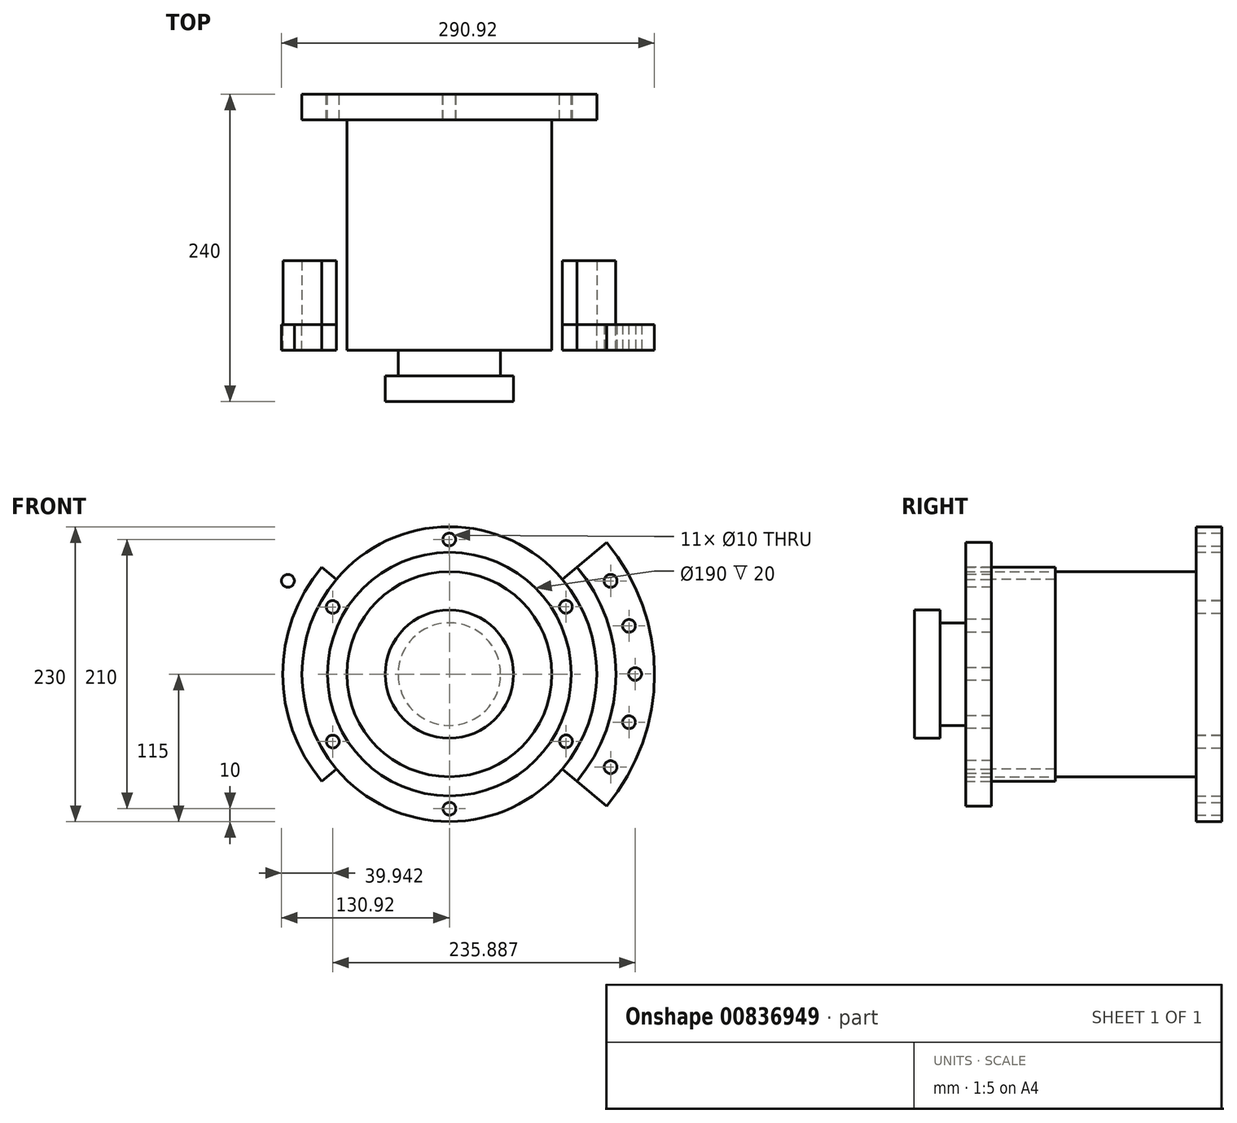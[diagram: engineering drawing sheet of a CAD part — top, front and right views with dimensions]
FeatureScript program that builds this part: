
annotation { "Feature Type Name" : "Feature", "Feature Type Description" : "" }
export const myFeature = defineFeature(function(context is Context, id is Id, definition is map)
    precondition{}
    {
        {
            var Q0;
            Q0=qCreatedBy(makeId("Front.planeOp"),FACE);
            var sketch = newSketch(context, id + "F0", { "sketchPlane" : qUnion([Q0])});
            skLineSegment(sketch, "E0", {"start": v(0, 0) * mm, "end": v(205.98, 0) * mm, "construction": true});
            skLineSegment(sketch, "E1", {"start": v(0, 0) * mm, "end": v(-190.1, -114.67) * mm, "construction": true});
            skLineSegment(sketch, "E2", {"start": v(189.9, 0.1) * mm, "end": v(-190.1, 0.1) * mm, "construction": true});
            skLineSegment(sketch, "E3", {"start": v(-0.1, 0.1) * mm, "end": v(-0.1, 105) * mm, "construction": true});
            skLineSegment(sketch, "E4.MirrorCS", {"start": v(189.9, 179.16) * mm, "end": v(189.9, -114.67) * mm, "construction": true});
            skCircle(sketch, "E5", {"center": v(144.9, 0.1) * mm, "radius": 5 * mm});
            skCircle(sketch, "E6", {"center": v(140.11, 37.67) * mm, "radius": 5 * mm});
            skCircle(sketch, "E7", {"center": v(125.73, 72.75) * mm, "radius": 5 * mm});
            skCircle(sketch, "E8.MirrorC", {"center": v(140.11, -37.46) * mm, "radius": 5 * mm});
            skCircle(sketch, "E9.MirrorC", {"center": v(125.73, -72.54) * mm, "radius": 5 * mm});
            skCircle(sketch, "E10.MirrorC", {"center": v(-125.92, 72.75) * mm, "radius": 5 * mm});
            skCircle(sketch, "E11.MirrorC", {"center": v(-140.3, 37.67) * mm, "radius": 5 * mm});
            skCircle(sketch, "E12.MirrorC", {"center": v(-145.1, 0.1) * mm, "radius": 5 * mm});
            skCircle(sketch, "E13.MirrorC", {"center": v(-140.3, -37.46) * mm, "radius": 5 * mm});
            skCircle(sketch, "E14.MirrorC", {"center": v(-125.92, -72.54) * mm, "radius": 5 * mm});
            skCircle(sketch, "E15", {"center": v(-0.1, 0.1) * mm, "radius": 145 * mm, "construction": true});
            skArc(sketch, "E16", {"start": v(-99.77, 83.56) * mm, "mid": v(-130.1, 0.02) * mm, "end": v(-99.66, -83.47) * mm});
            skLineSegment(sketch, "E17", {"start": v(79.9, 102.57) * mm, "end": v(79.9, 160.1) * mm, "construction": true});
            skLineSegment(sketch, "E18", {"start": v(79.9, 160.1) * mm, "end": v(-0.1, 160.1) * mm, "construction": true});
            skLineSegment(sketch, "E19.MirrorCS", {"start": v(-80.1, 160.1) * mm, "end": v(-0.1, 160.1) * mm, "construction": true});
            skLineSegment(sketch, "E20.MirrorCS", {"start": v(-80.1, 102.57) * mm, "end": v(-80.1, 160.1) * mm, "construction": true});
            skPoint(sketch, "E21.orphan", {"position": v(-80.1, 94.53) * mm});
            skPoint(sketch, "E22.orphan", {"position": v(79.9, 94.53) * mm});
            skLineSegment(sketch, "E23", {"start": v(-0.1, 0.1) * mm, "end": v(140.11, 37.67) * mm, "construction": true});
            skLineSegment(sketch, "E24", {"start": v(-0.1, 0.1) * mm, "end": v(125.73, 72.75) * mm, "construction": true});
            skCircle(sketch, "E25", {"center": v(0, 0) * mm, "radius": 65 * mm, "construction": true});
            skCircle(sketch, "E26", {"center": v(0, 0) * mm, "radius": 105 * mm, "construction": true});
            skCircle(sketch, "E27", {"center": v(-0.1, 105) * mm, "radius": 5 * mm});
            skCircle(sketch, "E28.1.0", {"center": v(-90.98, 52.42) * mm, "radius": 5 * mm});
            skCircle(sketch, "E28.2.0", {"center": v(-90.89, -52.58) * mm, "radius": 5 * mm});
            skCircle(sketch, "E28.3.0", {"center": v(0.1, -105) * mm, "radius": 5 * mm});
            skCircle(sketch, "E28.4.0", {"center": v(90.98, -52.42) * mm, "radius": 5 * mm});
            skCircle(sketch, "E28.5.0", {"center": v(90.89, 52.58) * mm, "radius": 5 * mm});
            skCircle(sketch, "E29", {"center": v(0, 0) * mm, "radius": 50 * mm});
            skLineSegment(sketch, "E30.trimOffspring", {"start": v(99.58, 83.56) * mm, "end": v(122.57, 102.85) * mm});
            skLineSegment(sketch, "E31.MirrorCS", {"start": v(99.48, -83.47) * mm, "end": v(122.57, -102.85) * mm});
            skArc(sketch, "E32.trimOffspring", {"start": v(122.57, -102.85) * mm, "mid": v(160, 0) * mm, "end": v(122.57, 102.85) * mm});
            skPoint(sketch, "E33.orphan", {"position": v(80.43, 67.5) * mm});
            skPoint(sketch, "E34.orphan", {"position": v(80.43, -67.5) * mm});
            skArc(sketch, "E35.MirrorCS", {"start": v(-122.75, -102.85) * mm, "mid": v(-160.18, 0) * mm, "end": v(-122.75, 102.85) * mm});
            skLineSegment(sketch, "E36.MirrorCS", {"start": v(-99.77, 83.56) * mm, "end": v(-122.75, 102.85) * mm});
            skLineSegment(sketch, "E37.MirrorCS", {"start": v(-99.66, -83.47) * mm, "end": v(-122.75, -102.85) * mm});
            skPoint(sketch, "E38.orphan", {"position": v(79.9, 102.57) * mm});
            skArc(sketch, "E39.trimOffspring", {"start": v(-99.66, -83.47) * mm, "mid": v(-129.38, 13.7) * mm, "end": v(-80.1, 102.57) * mm, "construction": true});
            skArc(sketch, "E40.MirrorCS", {"start": v(99.48, -83.47) * mm, "mid": v(129.9, 0.02) * mm, "end": v(99.58, 83.56) * mm});
            skCircle(sketch, "E41", {"center": v(0, 0) * mm, "radius": 115 * mm});
            skCircle(sketch, "E42", {"center": v(0, 0) * mm, "radius": 95 * mm});
            skSolve(sketch);
        }
        {
            var Q0;
            Q0=makeQuery(id+"F0.imprint","IMPRINT",FACE,{"disambiguationData":[TD([[makeQuery(id+"F0.imprint","IMPRINT",EDGE,{"derivedFrom":sQuery(id+"F0.wireOp",EDGE,"E5")}),-1.0]])]});
            var Q1;
            Q1=makeQuery(id+"F0.imprint","IMPRINT",FACE,{"disambiguationData":[TD([[makeQuery(id+"F0.imprint","IMPRINT",EDGE,{"derivedFrom":sQuery(id+"F0.wireOp",EDGE,"E10.MirrorC")}),1.0]])]});
            extrude(context, id + "F1", {"entities" : qUnion([Q0, Q1]), "oppositeDirection" : true, "depth" : 20 * mm, "offsetDistance" : 25 * mm});
        }
        {
            var Q0;
            Q0=makeQuery(id+"F1.opExtrude","CAP_FACE",FACE,{"disambiguationData":[OSD([sQuery(id+"F0.wireOp",EDGE,"E5"),sQuery(id+"F0.wireOp",EDGE,"E6"),sQuery(id+"F0.wireOp",EDGE,"E7"),sQuery(id+"F0.wireOp",EDGE,"E8.MirrorC"),sQuery(id+"F0.wireOp",EDGE,"E9.MirrorC"),sQuery(id+"F0.wireOp",EDGE,"E30.trimOffspring"),sQuery(id+"F0.wireOp",EDGE,"E31.MirrorCS"),sQuery(id+"F0.wireOp",EDGE,"E32.trimOffspring"),sQuery(id+"F0.wireOp",EDGE,"E40.MirrorCS")])],"isStart":false});
            cPlane(context, id + "F2", {"entities" : qUnion([Q0]), "cplaneType" : CPlaneType.OFFSET, "offset" : 180 * mm, "width" : 150 * mm, "height" : 150 * mm});
        }
        {
            var Q0;
            Q0=qCreatedBy(id+"F2.planeOp",FACE);
            var sketch = newSketch(context, id + "F3", { "sketchPlane" : qUnion([Q0])});
            skCircle(sketch, "E43.0", {"center": v(0, 0) * mm, "radius": 115 * mm});
            skCircle(sketch, "E44.0", {"center": v(0, 0) * mm, "radius": 95 * mm});
            skCircle(sketch, "E45.0", {"center": v(0, 0) * mm, "radius": 105 * mm, "construction": true});
            skCircle(sketch, "E46.0", {"center": v(0.1, 105) * mm, "radius": 5 * mm});
            skCircle(sketch, "E47.0", {"center": v(90.98, 52.42) * mm, "radius": 5 * mm});
            skCircle(sketch, "E48.0", {"center": v(90.89, -52.58) * mm, "radius": 5 * mm});
            skCircle(sketch, "E49.0", {"center": v(-90.89, 52.58) * mm, "radius": 5 * mm});
            skCircle(sketch, "E50.0", {"center": v(-90.98, -52.42) * mm, "radius": 5 * mm});
            skCircle(sketch, "E51.0", {"center": v(-0.1, -105) * mm, "radius": 5 * mm});
            skSolve(sketch);
        }
        {
            var Q0;
            Q0=makeQuery(id+"F3.imprint","IMPRINT",FACE,{"disambiguationData":[TD([[makeQuery(id+"F3.imprint","IMPRINT",EDGE,{"derivedFrom":sQuery(id+"F3.wireOp",EDGE,"E43.0")}),-1.0]])]});
            var Q1;
            Q1=makeQuery(id+"F3.imprint","IMPRINT",FACE,{"disambiguationData":[TD([[makeQuery(id+"F3.imprint","IMPRINT",EDGE,{"derivedFrom":sQuery(id+"F3.wireOp",EDGE,"E44.0")}),-1.0]])]});
            extrude(context, id + "F4", {"entities" : qUnion([Q0, Q1]), "oppositeDirection" : true, "depth" : 20 * mm, "offsetDistance" : 25 * mm});
        }
        {
            var Q0;
            Q0=makeQuery(id+"F4.opExtrude","CAP_FACE",FACE,{"disambiguationData":[OSD([sQuery(id+"F3.wireOp",EDGE,"E43.0"),sQuery(id+"F3.wireOp",EDGE,"E46.0"),sQuery(id+"F3.wireOp",EDGE,"E47.0"),sQuery(id+"F3.wireOp",EDGE,"E48.0"),sQuery(id+"F3.wireOp",EDGE,"E49.0"),sQuery(id+"F3.wireOp",EDGE,"E50.0"),sQuery(id+"F3.wireOp",EDGE,"E51.0")])],"isStart":false});
            var sketch = newSketch(context, id + "F5", { "sketchPlane" : qUnion([Q0])});
            skCircle(sketch, "E52", {"center": v(0, 0) * mm, "radius": 80 * mm});
            skSolve(sketch);
        }
        {
            var Q0;
            Q0=makeQuery(id+"F5.imprint","IMPRINT",FACE,{"disambiguationData":[TD([[makeQuery(id+"F5.imprint","IMPRINT",EDGE,{"derivedFrom":sQuery(id+"F5.wireOp",EDGE,"E52")}),1.0]])]});
            extrude(context, id + "F6", {"entities" : qUnion([Q0]), "operationType" : NewBodyOperationType.ADD, "depth" : 180 * mm, "offsetDistance" : 25 * mm});
        }
        {
            var Q0;
            Q0=makeQuery(id+"F6.opExtrude","CAP_FACE",FACE,{"disambiguationData":[OSD([sQuery(id+"F5.wireOp",EDGE,"E52")])],"isStart":false});
            var sketch = newSketch(context, id + "F7", { "sketchPlane" : qUnion([Q0])});
            skCircle(sketch, "E53", {"center": v(0, 0) * mm, "radius": 50 * mm});
            skCircle(sketch, "E54", {"center": v(0, 0) * mm, "radius": 40 * mm});
            skSolve(sketch);
        }
        {
            var Q0;
            Q0 = qSketchRegion(id + "F7", true);
            var Q1;
            Q1=makeQuery(id+"F7.imprint","IMPRINT",FACE,{"disambiguationData":[TD([[makeQuery(id+"F7.imprint","IMPRINT",EDGE,{"derivedFrom":sQuery(id+"F7.wireOp",EDGE,"E54")}),1.0]])]});
            extrude(context, id + "F8", {"entities" : qUnion([Q0, Q1]), "operationType" : NewBodyOperationType.ADD, "depth" : 40 * mm, "offsetDistance" : 25 * mm});
        }
        {
            var Q0;
            Q0=makeQuery(id+"F7.imprint","IMPRINT",FACE,{"disambiguationData":[TD([[makeQuery(id+"F7.imprint","IMPRINT",EDGE,{"derivedFrom":sQuery(id+"F7.wireOp",EDGE,"E53")}),1.0]])]});
            extrude(context, id + "F9", {"entities" : qUnion([Q0]), "operationType" : NewBodyOperationType.REMOVE, "depth" : 20 * mm, "offsetDistance" : 25 * mm});
        }
        {
            var Q0;
            Q0=makeQuery(id+"F1.opExtrude","CAP_FACE",FACE,{"disambiguationData":[OSD([sQuery(id+"F0.wireOp",EDGE,"E5"),sQuery(id+"F0.wireOp",EDGE,"E6"),sQuery(id+"F0.wireOp",EDGE,"E7"),sQuery(id+"F0.wireOp",EDGE,"E8.MirrorC"),sQuery(id+"F0.wireOp",EDGE,"E9.MirrorC"),sQuery(id+"F0.wireOp",EDGE,"E30.trimOffspring"),sQuery(id+"F0.wireOp",EDGE,"E31.MirrorCS"),sQuery(id+"F0.wireOp",EDGE,"E32.trimOffspring"),sQuery(id+"F0.wireOp",EDGE,"E40.MirrorCS")])],"isStart":false});
            var sketch = newSketch(context, id + "F10", { "sketchPlane" : qUnion([Q0])});
            skLineSegment(sketch, "E55", {"start": v(-99.58, 83.56) * mm, "end": v(-88.1, 73.92) * mm});
            skLineSegment(sketch, "E56", {"start": v(-88.1, -73.92) * mm, "end": v(-99.48, -83.47) * mm});
            skArc(sketch, "E57", {"start": v(-88.1, -73.92) * mm, "mid": v(-115, 0) * mm, "end": v(-88.1, 73.92) * mm});
            skArc(sketch, "E58", {"start": v(-99.48, -83.47) * mm, "mid": v(-129.86, 0) * mm, "end": v(-99.48, 83.47) * mm});
            skArc(sketch, "E59.MirrorCS", {"start": v(99.48, -83.47) * mm, "mid": v(129.86, 0) * mm, "end": v(99.48, 83.47) * mm});
            skLineSegment(sketch, "E60.MirrorCS", {"start": v(99.58, 83.56) * mm, "end": v(88.1, 73.92) * mm});
            skArc(sketch, "E61.MirrorCS", {"start": v(88.1, -73.92) * mm, "mid": v(115, 0) * mm, "end": v(88.1, 73.92) * mm});
            skLineSegment(sketch, "E62.MirrorCS", {"start": v(88.1, -73.92) * mm, "end": v(99.48, -83.47) * mm});
            skSolve(sketch);
        }
        {
            var Q0;
            {var subQ0=sQuery(id+"F10.wireOp",EDGE,"E59.MirrorCS");Q0=makeQuery(id+"F10.imprint","IMPRINT",FACE,{"disambiguationData":[TD([[makeQuery(id+"F10.imprint","IMPRINT",EDGE,{"derivedFrom":subQ0}),1.0]])]});}
            var Q1;
            Q1=makeQuery(id+"F10.imprint","IMPRINT",FACE,{"disambiguationData":[TD([[makeQuery(id+"F10.imprint","IMPRINT",EDGE,{"derivedFrom":sQuery(id+"F10.wireOp",EDGE,"E56")}),-1.0]])]});
            extrude(context, id + "F11", {"entities" : qUnion([Q0, Q1]), "oppositeDirection" : true, "depth" : 20 * mm, "offsetDistance" : 25 * mm});
        }
        {
            var Q0;
            {var subQ0=sQuery(id+"F10.wireOp",EDGE,"E59.MirrorCS");Q0=makeQuery(id+"F10.imprint","IMPRINT",FACE,{"disambiguationData":[TD([[makeQuery(id+"F10.imprint","IMPRINT",EDGE,{"derivedFrom":subQ0}),1.0]])]});}
            var Q1;
            Q1=makeQuery(id+"F10.imprint","IMPRINT",FACE,{"disambiguationData":[TD([[makeQuery(id+"F10.imprint","IMPRINT",EDGE,{"derivedFrom":sQuery(id+"F10.wireOp",EDGE,"E56")}),-1.0]])]});
            extrude(context, id + "F12", {"entities" : qUnion([Q0, Q1]), "depth" : 50 * mm, "offsetDistance" : 25 * mm});
        }
    });
